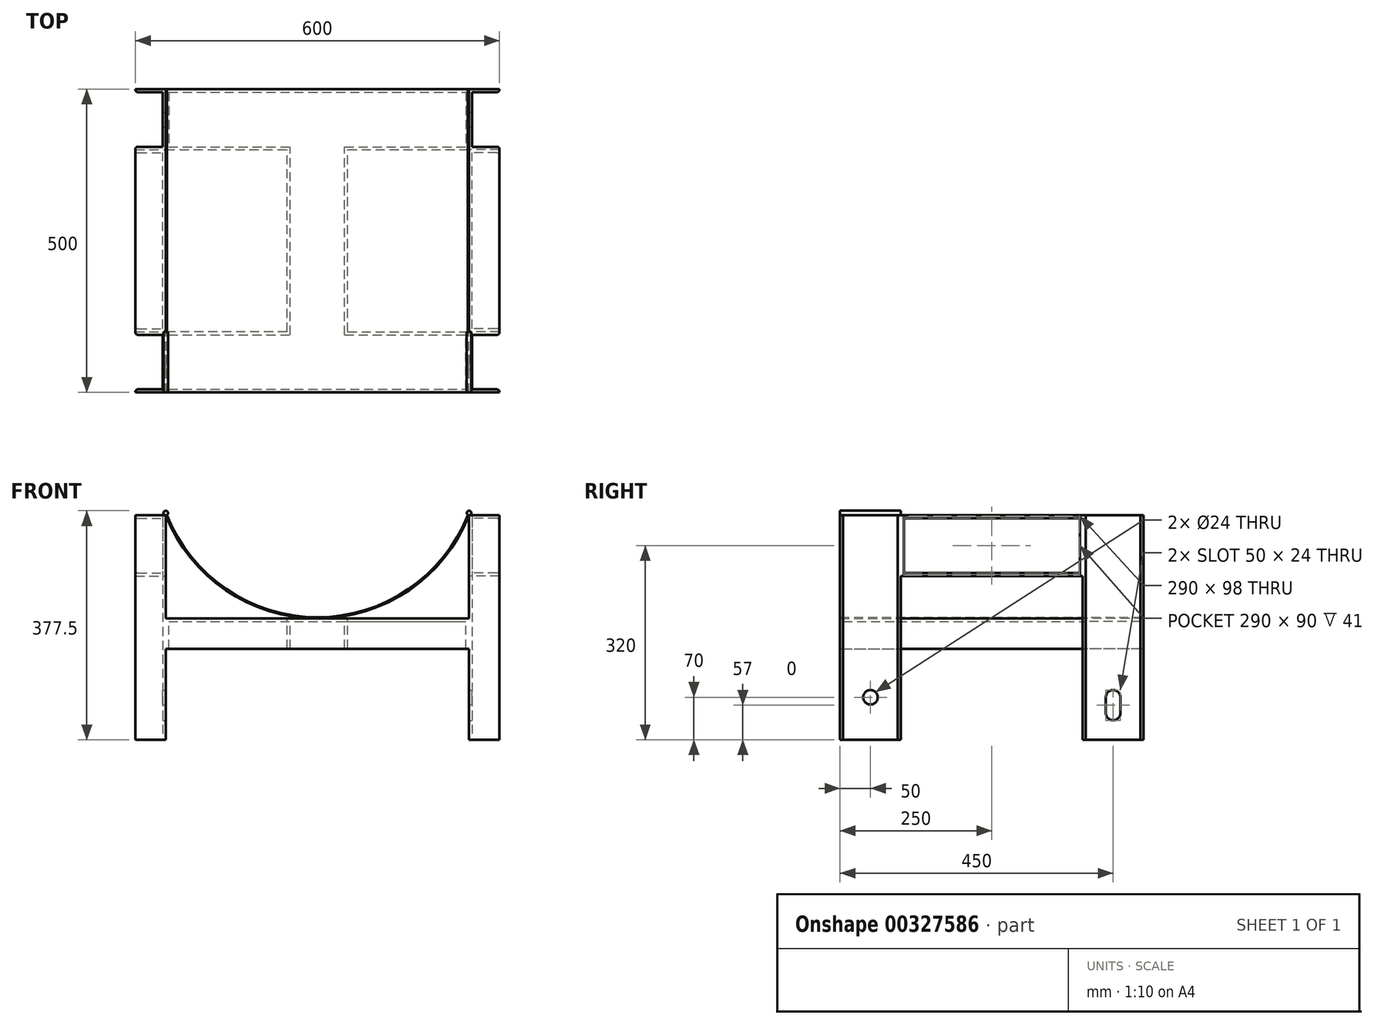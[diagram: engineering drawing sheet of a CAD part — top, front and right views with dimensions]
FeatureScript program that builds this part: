
annotation { "Feature Type Name" : "Feature", "Feature Type Description" : "" }
export const myFeature = defineFeature(function(context is Context, id is Id, definition is map)
    precondition{}
    {
        {
            var Q0;
            Q0=qCreatedBy(makeId("Top.planeOp"),FACE);
            var sketch = newSketch(context, id + "F0", { "sketchPlane" : qUnion([Q0])});
            skLineSegment(sketch, "E0.bottom", {"start": v(250, 250) * mm, "end": v(-250, 250) * mm, "construction": true});
            skLineSegment(sketch, "E0.top", {"start": v(250, -250) * mm, "end": v(-250, -250) * mm, "construction": true});
            skLineSegment(sketch, "E0.left", {"start": v(250, 250) * mm, "end": v(250, -250) * mm, "construction": true});
            skLineSegment(sketch, "E0.right", {"start": v(-250, 250) * mm, "end": v(-250, -250) * mm, "construction": true});
            skPoint(sketch, "E0.middle", {"position": v(0, 0) * mm});
            skLineSegment(sketch, "E1.bottom", {"start": v(-250, 250) * mm, "end": v(250, 250) * mm});
            skLineSegment(sketch, "E1.top", {"start": v(-250, 150) * mm, "end": v(250, 150) * mm});
            skLineSegment(sketch, "E1.left", {"start": v(-250, 250) * mm, "end": v(-250, 150) * mm});
            skLineSegment(sketch, "E1.right", {"start": v(250, 250) * mm, "end": v(250, 150) * mm});
            skLineSegment(sketch, "E2", {"start": v(0, 0) * mm, "end": v(0, 150) * mm, "construction": true});
            skLineSegment(sketch, "E3.bottom", {"start": v(50, 0) * mm, "end": v(-50, 0) * mm});
            skLineSegment(sketch, "E3.top", {"start": v(50, 150) * mm, "end": v(-50, 150) * mm});
            skLineSegment(sketch, "E3.left", {"start": v(50, 0) * mm, "end": v(50, 150) * mm});
            skLineSegment(sketch, "E3.right", {"start": v(-50, 0) * mm, "end": v(-50, 150) * mm});
            skPoint(sketch, "E3.middle", {"position": v(0, 75) * mm});
            skLineSegment(sketch, "E4.MirrorCS", {"start": v(50, 0) * mm, "end": v(50, -150) * mm});
            skLineSegment(sketch, "E5.MirrorCS", {"start": v(-50, 0) * mm, "end": v(-50, -150) * mm});
            skLineSegment(sketch, "E6.MirrorCS", {"start": v(50, -150) * mm, "end": v(-50, -150) * mm});
            skLineSegment(sketch, "E7.MirrorCS", {"start": v(-250, -150) * mm, "end": v(250, -150) * mm});
            skLineSegment(sketch, "E8.MirrorCS", {"start": v(-250, -250) * mm, "end": v(250, -250) * mm});
            skLineSegment(sketch, "E9.MirrorCS", {"start": v(-250, -250) * mm, "end": v(-250, -150) * mm});
            skLineSegment(sketch, "E10.MirrorCS", {"start": v(250, -250) * mm, "end": v(250, -150) * mm});
            skLineSegment(sketch, "E11.bottom", {"start": v(250, -250) * mm, "end": v(300, -250) * mm});
            skLineSegment(sketch, "E11.top", {"start": v(250, -150) * mm, "end": v(300, -150) * mm});
            skLineSegment(sketch, "E11.right", {"start": v(300, -250) * mm, "end": v(300, -249) * mm});
            skLineSegment(sketch, "E12", {"start": v(296, -155) * mm, "end": v(255, -155) * mm});
            skLineSegment(sketch, "E13", {"start": v(255, -155) * mm, "end": v(255, -245) * mm});
            skLineSegment(sketch, "E14", {"start": v(255, -245) * mm, "end": v(296, -245) * mm});
            skLineSegment(sketch, "E15.trimOffspring", {"start": v(300, -151) * mm, "end": v(300, -150) * mm});
            skPoint(sketch, "E16.visualSharp", {"position": v(300, -155) * mm});
            skArc(sketch, "E16.filletArc", {"start": v(296, -155) * mm, "mid": v(298.83, -153.83) * mm, "end": v(300, -151) * mm});
            skPoint(sketch, "E17.visualSharp", {"position": v(300, -245) * mm});
            skArc(sketch, "E17.filletArc", {"start": v(300, -249) * mm, "mid": v(298.83, -246.17) * mm, "end": v(296, -245) * mm});
            skLineSegment(sketch, "E18.MirrorCS", {"start": v(255, 155) * mm, "end": v(255, 245) * mm});
            skLineSegment(sketch, "E19.MirrorCS", {"start": v(250, 150) * mm, "end": v(300, 150) * mm});
            skLineSegment(sketch, "E20.MirrorCS", {"start": v(296, 155) * mm, "end": v(255, 155) * mm});
            skLineSegment(sketch, "E21.MirrorCS", {"start": v(250, 250) * mm, "end": v(300, 250) * mm});
            skLineSegment(sketch, "E22.MirrorCS", {"start": v(255, 245) * mm, "end": v(296, 245) * mm});
            skArc(sketch, "E23.MirrorCS", {"start": v(300, 249) * mm, "mid": v(298.83, 246.17) * mm, "end": v(296, 245) * mm});
            skLineSegment(sketch, "E24.MirrorCS", {"start": v(300, 250) * mm, "end": v(300, 249) * mm});
            skArc(sketch, "E25.MirrorCS", {"start": v(296, 155) * mm, "mid": v(298.83, 153.83) * mm, "end": v(300, 151) * mm});
            skLineSegment(sketch, "E26.MirrorCS", {"start": v(300, 151) * mm, "end": v(300, 150) * mm});
            skLineSegment(sketch, "E27.MirrorCS", {"start": v(-250, 150) * mm, "end": v(-300, 150) * mm});
            skLineSegment(sketch, "E28.MirrorCS", {"start": v(-296, 155) * mm, "end": v(-255, 155) * mm});
            skLineSegment(sketch, "E29.MirrorCS", {"start": v(-250, 250) * mm, "end": v(-300, 250) * mm});
            skLineSegment(sketch, "E30.MirrorCS", {"start": v(-255, 245) * mm, "end": v(-296, 245) * mm});
            skLineSegment(sketch, "E31.MirrorCS", {"start": v(-255, 155) * mm, "end": v(-255, 245) * mm});
            skArc(sketch, "E32.MirrorCS", {"start": v(-296, 155) * mm, "mid": v(-298.83, 153.83) * mm, "end": v(-300, 151) * mm});
            skArc(sketch, "E33.MirrorCS", {"start": v(-300, 249) * mm, "mid": v(-298.83, 246.17) * mm, "end": v(-296, 245) * mm});
            skLineSegment(sketch, "E34.MirrorCS", {"start": v(-300, 250) * mm, "end": v(-300, 249) * mm});
            skLineSegment(sketch, "E35.MirrorCS", {"start": v(-300, 151) * mm, "end": v(-300, 150) * mm});
            skLineSegment(sketch, "E36.MirrorCS", {"start": v(-250, -250) * mm, "end": v(-300, -250) * mm});
            skLineSegment(sketch, "E37.MirrorCS", {"start": v(-255, -245) * mm, "end": v(-296, -245) * mm});
            skLineSegment(sketch, "E38.MirrorCS", {"start": v(-296, -155) * mm, "end": v(-255, -155) * mm});
            skLineSegment(sketch, "E39.MirrorCS", {"start": v(-250, -150) * mm, "end": v(-300, -150) * mm});
            skArc(sketch, "E40.MirrorCS", {"start": v(-300, -249) * mm, "mid": v(-298.83, -246.17) * mm, "end": v(-296, -245) * mm});
            skLineSegment(sketch, "E41.MirrorCS", {"start": v(-300, -250) * mm, "end": v(-300, -249) * mm});
            skArc(sketch, "E42.MirrorCS", {"start": v(-296, -155) * mm, "mid": v(-298.83, -153.83) * mm, "end": v(-300, -151) * mm});
            skLineSegment(sketch, "E43.MirrorCS", {"start": v(-300, -151) * mm, "end": v(-300, -150) * mm});
            skLineSegment(sketch, "E44.MirrorCS", {"start": v(-255, -155) * mm, "end": v(-255, -245) * mm});
            skSolve(sketch);
        }
        {
            var Q0;
            Q0=makeQuery(id+"F0.imprint","IMPRINT",FACE,{"disambiguationData":[TD([[makeQuery(id+"F0.imprint","IMPRINT",EDGE,{"derivedFrom":sQuery(id+"F0.wireOp",EDGE,"E1.bottom")}),-1.0]])]});
            var Q1;
            Q1=makeQuery(id+"F0.imprint","IMPRINT",FACE,{"disambiguationData":[TD([[makeQuery(id+"F0.imprint","IMPRINT",EDGE,{"derivedFrom":sQuery(id+"F0.wireOp",EDGE,"E3.bottom")}),-1.0]])]});
            var Q2;
            Q2=makeQuery(id+"F0.imprint","IMPRINT",FACE,{"disambiguationData":[TD([[makeQuery(id+"F0.imprint","IMPRINT",EDGE,{"derivedFrom":sQuery(id+"F0.wireOp",EDGE,"E3.bottom")}),1.0]])]});
            var Q3;
            Q3=makeQuery(id+"F0.imprint","IMPRINT",FACE,{"disambiguationData":[TD([[makeQuery(id+"F0.imprint","IMPRINT",EDGE,{"derivedFrom":sQuery(id+"F0.wireOp",EDGE,"E8.MirrorCS")}),1.0]])]});
            extrude(context, id + "F1", {"entities" : qUnion([Q0, Q1, Q2, Q3]), "oppositeDirection" : true, "depth" : 50 * mm});
        }
        {
            var Q0;
            Q0=makeQuery(id+"F1.opExtrude","CAP_FACE",FACE,{"disambiguationData":[OSD([sQuery(id+"F0.wireOp",EDGE,"E1.bottom"),sQuery(id+"F0.wireOp",EDGE,"E1.top"),sQuery(id+"F0.wireOp",EDGE,"E1.left"),sQuery(id+"F0.wireOp",EDGE,"E1.right"),sQuery(id+"F0.wireOp",EDGE,"E3.left"),sQuery(id+"F0.wireOp",EDGE,"E3.right"),sQuery(id+"F0.wireOp",EDGE,"E4.MirrorCS"),sQuery(id+"F0.wireOp",EDGE,"E5.MirrorCS"),sQuery(id+"F0.wireOp",EDGE,"E7.MirrorCS"),sQuery(id+"F0.wireOp",EDGE,"E8.MirrorCS"),sQuery(id+"F0.wireOp",EDGE,"E9.MirrorCS"),sQuery(id+"F0.wireOp",EDGE,"E10.MirrorCS")])],"isStart":false});
            shell(context, id + "F2", {"entities" : qUnion([Q0]), "thickness" : 5 * mm});
        }
        {
            var Q0;
            Q0=makeQuery(id+"F0.imprint","IMPRINT",FACE,{"disambiguationData":[TD([[makeQuery(id+"F0.imprint","IMPRINT",EDGE,{"derivedFrom":sQuery(id+"F0.wireOp",EDGE,"E9.MirrorCS")}),1.0]])]});
            var Q1;
            Q1=makeQuery(id+"F0.imprint","IMPRINT",FACE,{"disambiguationData":[TD([[makeQuery(id+"F0.imprint","IMPRINT",EDGE,{"derivedFrom":sQuery(id+"F0.wireOp",EDGE,"E11.bottom")}),1.0]])]});
            var Q2;
            Q2=makeQuery(id+"F0.imprint","IMPRINT",FACE,{"disambiguationData":[TD([[makeQuery(id+"F0.imprint","IMPRINT",EDGE,{"derivedFrom":sQuery(id+"F0.wireOp",EDGE,"E1.right")}),1.0]])]});
            var Q3;
            Q3=makeQuery(id+"F0.imprint","IMPRINT",FACE,{"disambiguationData":[TD([[makeQuery(id+"F0.imprint","IMPRINT",EDGE,{"derivedFrom":sQuery(id+"F0.wireOp",EDGE,"E1.left")}),-1.0]])]});
            extrude(context, id + "F3", {"entities" : qUnion([Q0, Q1, Q2, Q3]), "depth" : 170 * mm});
        }
        {
            var Q0;
            Q0=makeQuery(id+"F0.imprint","IMPRINT",FACE,{"disambiguationData":[TD([[makeQuery(id+"F0.imprint","IMPRINT",EDGE,{"derivedFrom":sQuery(id+"F0.wireOp",EDGE,"E9.MirrorCS")}),1.0]])]});
            var Q1;
            Q1=makeQuery(id+"F0.imprint","IMPRINT",FACE,{"disambiguationData":[TD([[makeQuery(id+"F0.imprint","IMPRINT",EDGE,{"derivedFrom":sQuery(id+"F0.wireOp",EDGE,"E11.bottom")}),1.0]])]});
            var Q2;
            Q2=makeQuery(id+"F0.imprint","IMPRINT",FACE,{"disambiguationData":[TD([[makeQuery(id+"F0.imprint","IMPRINT",EDGE,{"derivedFrom":sQuery(id+"F0.wireOp",EDGE,"E1.right")}),1.0]])]});
            var Q3;
            Q3=makeQuery(id+"F0.imprint","IMPRINT",FACE,{"disambiguationData":[TD([[makeQuery(id+"F0.imprint","IMPRINT",EDGE,{"derivedFrom":sQuery(id+"F0.wireOp",EDGE,"E1.left")}),-1.0]])]});
            extrude(context, id + "F4", {"entities" : qUnion([Q0, Q1, Q2, Q3]), "oppositeDirection" : true, "depth" : 200 * mm});
        }
        {
            var Q0;
            Q0=makeQuery(id+"F3.opExtrude","SWEPT_BODY",BODY,{"disambiguationData":[OSD([sQuery(id+"F0.wireOp",EDGE,"E11.bottom"),sQuery(id+"F0.wireOp",EDGE,"E11.top"),sQuery(id+"F0.wireOp",EDGE,"E10.MirrorCS"),sQuery(id+"F0.wireOp",EDGE,"E11.right"),sQuery(id+"F0.wireOp",EDGE,"E12"),sQuery(id+"F0.wireOp",EDGE,"E13"),sQuery(id+"F0.wireOp",EDGE,"E14"),sQuery(id+"F0.wireOp",EDGE,"E15.trimOffspring"),sQuery(id+"F0.wireOp",EDGE,"E16.filletArc"),sQuery(id+"F0.wireOp",EDGE,"E17.filletArc")])]});
            var Q1;
            Q1=makeQuery(id+"F4.opExtrude","SWEPT_BODY",BODY,{"disambiguationData":[OSD([sQuery(id+"F0.wireOp",EDGE,"E11.bottom"),sQuery(id+"F0.wireOp",EDGE,"E11.top"),sQuery(id+"F0.wireOp",EDGE,"E10.MirrorCS"),sQuery(id+"F0.wireOp",EDGE,"E11.right"),sQuery(id+"F0.wireOp",EDGE,"E12"),sQuery(id+"F0.wireOp",EDGE,"E13"),sQuery(id+"F0.wireOp",EDGE,"E14"),sQuery(id+"F0.wireOp",EDGE,"E15.trimOffspring"),sQuery(id+"F0.wireOp",EDGE,"E16.filletArc"),sQuery(id+"F0.wireOp",EDGE,"E17.filletArc")])]});
            var Q2;
            Q2=makeQuery(id+"F3.opExtrude","SWEPT_BODY",BODY,{"disambiguationData":[OSD([sQuery(id+"F0.wireOp",EDGE,"E1.right"),sQuery(id+"F0.wireOp",EDGE,"E18.MirrorCS"),sQuery(id+"F0.wireOp",EDGE,"E19.MirrorCS"),sQuery(id+"F0.wireOp",EDGE,"E20.MirrorCS"),sQuery(id+"F0.wireOp",EDGE,"E21.MirrorCS"),sQuery(id+"F0.wireOp",EDGE,"E22.MirrorCS"),sQuery(id+"F0.wireOp",EDGE,"E23.MirrorCS"),sQuery(id+"F0.wireOp",EDGE,"E24.MirrorCS"),sQuery(id+"F0.wireOp",EDGE,"E25.MirrorCS"),sQuery(id+"F0.wireOp",EDGE,"E26.MirrorCS")])]});
            var Q3;
            Q3=makeQuery(id+"F4.opExtrude","SWEPT_BODY",BODY,{"disambiguationData":[OSD([sQuery(id+"F0.wireOp",EDGE,"E1.right"),sQuery(id+"F0.wireOp",EDGE,"E18.MirrorCS"),sQuery(id+"F0.wireOp",EDGE,"E19.MirrorCS"),sQuery(id+"F0.wireOp",EDGE,"E20.MirrorCS"),sQuery(id+"F0.wireOp",EDGE,"E21.MirrorCS"),sQuery(id+"F0.wireOp",EDGE,"E22.MirrorCS"),sQuery(id+"F0.wireOp",EDGE,"E23.MirrorCS"),sQuery(id+"F0.wireOp",EDGE,"E24.MirrorCS"),sQuery(id+"F0.wireOp",EDGE,"E25.MirrorCS"),sQuery(id+"F0.wireOp",EDGE,"E26.MirrorCS")])]});
            var Q4;
            Q4=makeQuery(id+"F3.opExtrude","SWEPT_BODY",BODY,{"disambiguationData":[OSD([sQuery(id+"F0.wireOp",EDGE,"E9.MirrorCS"),sQuery(id+"F0.wireOp",EDGE,"E36.MirrorCS"),sQuery(id+"F0.wireOp",EDGE,"E37.MirrorCS"),sQuery(id+"F0.wireOp",EDGE,"E38.MirrorCS"),sQuery(id+"F0.wireOp",EDGE,"E39.MirrorCS"),sQuery(id+"F0.wireOp",EDGE,"E40.MirrorCS"),sQuery(id+"F0.wireOp",EDGE,"E41.MirrorCS"),sQuery(id+"F0.wireOp",EDGE,"E42.MirrorCS"),sQuery(id+"F0.wireOp",EDGE,"E43.MirrorCS"),sQuery(id+"F0.wireOp",EDGE,"E44.MirrorCS")])]});
            var Q5;
            Q5=makeQuery(id+"F4.opExtrude","SWEPT_BODY",BODY,{"disambiguationData":[OSD([sQuery(id+"F0.wireOp",EDGE,"E9.MirrorCS"),sQuery(id+"F0.wireOp",EDGE,"E36.MirrorCS"),sQuery(id+"F0.wireOp",EDGE,"E37.MirrorCS"),sQuery(id+"F0.wireOp",EDGE,"E38.MirrorCS"),sQuery(id+"F0.wireOp",EDGE,"E39.MirrorCS"),sQuery(id+"F0.wireOp",EDGE,"E40.MirrorCS"),sQuery(id+"F0.wireOp",EDGE,"E41.MirrorCS"),sQuery(id+"F0.wireOp",EDGE,"E42.MirrorCS"),sQuery(id+"F0.wireOp",EDGE,"E43.MirrorCS"),sQuery(id+"F0.wireOp",EDGE,"E44.MirrorCS")])]});
            var Q6;
            Q6=makeQuery(id+"F4.opExtrude","SWEPT_BODY",BODY,{"disambiguationData":[OSD([sQuery(id+"F0.wireOp",EDGE,"E1.left"),sQuery(id+"F0.wireOp",EDGE,"E27.MirrorCS"),sQuery(id+"F0.wireOp",EDGE,"E28.MirrorCS"),sQuery(id+"F0.wireOp",EDGE,"E29.MirrorCS"),sQuery(id+"F0.wireOp",EDGE,"E30.MirrorCS"),sQuery(id+"F0.wireOp",EDGE,"E31.MirrorCS"),sQuery(id+"F0.wireOp",EDGE,"E32.MirrorCS"),sQuery(id+"F0.wireOp",EDGE,"E33.MirrorCS"),sQuery(id+"F0.wireOp",EDGE,"E34.MirrorCS"),sQuery(id+"F0.wireOp",EDGE,"E35.MirrorCS")])]});
            var Q7;
            Q7=makeQuery(id+"F3.opExtrude","SWEPT_BODY",BODY,{"disambiguationData":[OSD([sQuery(id+"F0.wireOp",EDGE,"E1.left"),sQuery(id+"F0.wireOp",EDGE,"E27.MirrorCS"),sQuery(id+"F0.wireOp",EDGE,"E28.MirrorCS"),sQuery(id+"F0.wireOp",EDGE,"E29.MirrorCS"),sQuery(id+"F0.wireOp",EDGE,"E30.MirrorCS"),sQuery(id+"F0.wireOp",EDGE,"E31.MirrorCS"),sQuery(id+"F0.wireOp",EDGE,"E32.MirrorCS"),sQuery(id+"F0.wireOp",EDGE,"E33.MirrorCS"),sQuery(id+"F0.wireOp",EDGE,"E34.MirrorCS"),sQuery(id+"F0.wireOp",EDGE,"E35.MirrorCS")])]});
            var Q8;
            Q8=makeQuery(id+"F1.opExtrude","SWEPT_BODY",BODY,{"disambiguationData":[OSD([sQuery(id+"F0.wireOp",EDGE,"E1.bottom"),sQuery(id+"F0.wireOp",EDGE,"E1.top"),sQuery(id+"F0.wireOp",EDGE,"E1.left"),sQuery(id+"F0.wireOp",EDGE,"E1.right"),sQuery(id+"F0.wireOp",EDGE,"E3.left"),sQuery(id+"F0.wireOp",EDGE,"E3.right"),sQuery(id+"F0.wireOp",EDGE,"E4.MirrorCS"),sQuery(id+"F0.wireOp",EDGE,"E5.MirrorCS"),sQuery(id+"F0.wireOp",EDGE,"E7.MirrorCS"),sQuery(id+"F0.wireOp",EDGE,"E8.MirrorCS"),sQuery(id+"F0.wireOp",EDGE,"E9.MirrorCS"),sQuery(id+"F0.wireOp",EDGE,"E10.MirrorCS")])]});
            booleanBodies(context, id + "F5", {"operationType" : BooleanOperationType.UNION, "tools" : qUnion([Q0, Q1, Q2, Q3, Q4, Q5, Q6, Q7, Q8])});
        }
        {
            var Q0;
            Q0=qCreatedBy(makeId("Front.planeOp"),FACE);
            var sketch = newSketch(context, id + "F6", { "sketchPlane" : qUnion([Q0])});
            skLineSegment(sketch, "E45.bottom", {"start": v(250, 170) * mm, "end": v(-250, 170) * mm, "construction": true});
            skLineSegment(sketch, "E45.top", {"start": v(250, -170) * mm, "end": v(-250, -170) * mm, "construction": true});
            skLineSegment(sketch, "E45.left", {"start": v(250, 170) * mm, "end": v(250, -170) * mm, "construction": true});
            skLineSegment(sketch, "E45.right", {"start": v(-250, 170) * mm, "end": v(-250, -170) * mm, "construction": true});
            skPoint(sketch, "E45.middle", {"position": v(0, 0) * mm});
            skArc(sketch, "E46", {"start": v(-250, 170) * mm, "mid": v(0, 0) * mm, "end": v(250, 170) * mm});
            skArc(sketch, "E47.0", {"start": v(-247.85, 170) * mm, "mid": v(0, 2) * mm, "end": v(247.85, 170) * mm});
            skLineSegment(sketch, "E48", {"start": v(247.85, 170) * mm, "end": v(250, 170) * mm});
            skLineSegment(sketch, "E49", {"start": v(-250, 170) * mm, "end": v(-247.85, 170) * mm});
            skSolve(sketch);
        }
        {
            var Q0;
            Q0=makeQuery(id+"F6.imprint","IMPRINT",FACE,{"disambiguationData":[TD([[makeQuery(id+"F6.imprint","IMPRINT",EDGE,{"derivedFrom":sQuery(id+"F6.wireOp",EDGE,"E46")}),1.0]])]});
            var Q1;
            Q1=makeQuery(id+"F6.imprint","IMPRINT",FACE,{"disambiguationData":[TD([[makeQuery(id+"F6.imprint","IMPRINT",EDGE,{"derivedFrom":sQuery(id+"F6.wireOp",EDGE,"KrNz5f9j-idMk-tH8w-1q6d-Px5I6zzqWWuj")}),1.0]])]});
            var Q2;
            Q2=makeQuery(id+"F6.imprint","IMPRINT",FACE,{"disambiguationData":[TD([[makeQuery(id+"F6.imprint","IMPRINT",EDGE,{"derivedFrom":sQuery(id+"F6.wireOp",EDGE,"515c8cf5-25ff-4abc-af07-5d9691053d920.MirrorC")}),-1.0]])]});
            extrude(context, id + "F7", {"entities" : qUnion([Q0, Q1, Q2]), "operationType" : NewBodyOperationType.ADD, "endBound" : BoundingType.SYMMETRIC, "depth" : 500 * mm});
        }
        {
            var Q0;
            Q0=makeQuery(id+"F3.opExtrude","SWEPT_FACE",FACE,{"disambiguationData":[OSD([sQuery(id+"F0.wireOp",EDGE,"E10.MirrorCS")])]});
            var sketch = newSketch(context, id + "F8", { "sketchPlane" : qUnion([Q0])});
            skLineSegment(sketch, "E50.bottom", {"start": v(150, 170) * mm, "end": v(-150, 170) * mm});
            skLineSegment(sketch, "E50.top", {"start": v(150, 70) * mm, "end": v(-150, 70) * mm});
            skLineSegment(sketch, "E50.left", {"start": v(150, 170) * mm, "end": v(150, 70) * mm});
            skLineSegment(sketch, "E50.right", {"start": v(-150, 170) * mm, "end": v(-150, 70) * mm});
            skSolve(sketch);
        }
        {
            var Q0;
            Q0=makeQuery(id+"F8.imprint","IMPRINT",FACE,{"disambiguationData":[TD([[makeQuery(id+"F8.imprint","IMPRINT",EDGE,{"derivedFrom":sQuery(id+"F8.wireOp",EDGE,"E50.bottom")}),1.0]])]});
            extrude(context, id + "F9", {"entities" : qUnion([Q0]), "oppositeDirection" : true, "depth" : 50 * mm});
        }
        {
            var Q0;
            Q0=makeQuery(id+"F9.opExtrude","CAP_FACE",FACE,{"disambiguationData":[OSD([sQuery(id+"F8.wireOp",EDGE,"E50.bottom"),sQuery(id+"F8.wireOp",EDGE,"E50.top"),sQuery(id+"F8.wireOp",EDGE,"E50.left"),sQuery(id+"F8.wireOp",EDGE,"E50.right")])],"isStart":false});
            shell(context, id + "F10", {"entities" : qUnion([Q0]), "thickness" : 5 * mm});
        }
        {
            var Q0;
            {var subQ0=sQuery(id+"F8.wireOp",EDGE,"E50.bottom");Q0=makeQuery(id+"F10.opShell","OFFSET_EDGE",EDGE,{"disambiguationData":[OSD([subQ0]),TDD([makeQuery(id+"F9.opExtrude","CAP_EDGE",EDGE,{"disambiguationData":[OSD([subQ0])],"isStart":false})])]});}
            var Q1;
            {var subQ0=sQuery(id+"F8.wireOp",EDGE,"E50.top");Q1=makeQuery(id+"F10.opShell","OFFSET_EDGE",EDGE,{"disambiguationData":[OSD([subQ0]),TDD([makeQuery(id+"F9.opExtrude","CAP_EDGE",EDGE,{"disambiguationData":[OSD([subQ0])],"isStart":false})])]});}
            fillet(context, id + "F11", {"entities" : qUnion([Q0, Q1]), "radius" : 4 * mm, "tangentPropagation" : true, "allowEdgeOverflow" : false});
        }
        {
            var Q0;
            Q0=makeQuery(id+"F9.opExtrude","SWEPT_BODY",BODY,{"disambiguationData":[OSD([sQuery(id+"F8.wireOp",EDGE,"E50.bottom"),sQuery(id+"F8.wireOp",EDGE,"E50.top"),sQuery(id+"F8.wireOp",EDGE,"E50.left"),sQuery(id+"F8.wireOp",EDGE,"E50.right")])]});
            var Q1;
            Q1=qCreatedBy(makeId("Right.planeOp"),FACE);
            mirror(context, id + "F12", {"operationType" : NewBodyOperationType.ADD, "entities" : qUnion([Q0]), "mirrorPlane" : qUnion([Q1])});
        }
        {
            var Q0;
            {var subQ0=sQuery(id+"F0.wireOp",EDGE,"E13");Q0=makeQuery(id+"F5.opBoolean","MERGE",FACE,{"derivedFrom":[makeQuery(id+"F3.opExtrude","SWEPT_FACE",FACE,{"disambiguationData":[OSD([subQ0])]}),makeQuery(id+"F4.opExtrude","SWEPT_FACE",FACE,{"disambiguationData":[OSD([subQ0])]})]});}
            var sketch = newSketch(context, id + "F13", { "sketchPlane" : qUnion([Q0])});
            skLineSegment(sketch, "E51", {"start": v(-200, -200) * mm, "end": v(-200, -130) * mm, "construction": true});
            skPoint(sketch, "E52", {"position": v(-200, -130) * mm});
            skLineSegment(sketch, "E53", {"start": v(-200, -200) * mm, "end": v(200, -200) * mm, "construction": true});
            skLineSegment(sketch, "E54", {"start": v(200, -200) * mm, "end": v(200, -143) * mm, "construction": true});
            skPoint(sketch, "E55", {"position": v(200, -143) * mm});
            skLineSegment(sketch, "E56.bottom", {"start": v(212, -118) * mm, "end": v(188, -118) * mm});
            skLineSegment(sketch, "E56.top", {"start": v(212, -168) * mm, "end": v(188, -168) * mm});
            skLineSegment(sketch, "E56.left", {"start": v(212, -118) * mm, "end": v(212, -168) * mm});
            skLineSegment(sketch, "E56.right", {"start": v(188, -118) * mm, "end": v(188, -168) * mm});
            skLineSegment(sketch, "E57", {"start": v(200, -118) * mm, "end": v(200, -130) * mm, "construction": true});
            skPoint(sketch, "E58.orphan", {"position": v(212, -130) * mm});
            skPoint(sketch, "E59.0.end.orphan", {"position": v(188, -130) * mm});
            skArc(sketch, "E60", {"start": v(212, -130) * mm, "mid": v(200, -118) * mm, "end": v(188, -130) * mm});
            skLineSegment(sketch, "E61", {"start": v(188, -143) * mm, "end": v(212, -143) * mm, "construction": true});
            skArc(sketch, "E62.MirrorCS", {"start": v(212, -156) * mm, "mid": v(200, -168) * mm, "end": v(188, -156) * mm});
            skSolve(sketch);
        }
        {
            var Q0;
            {var subQ0=sQuery(id+"F13.wireOp",EDGE,"E60");var subQ6=sQuery(id+"F13.wireOp",EDGE,"E56.left");var subQ7=makeQuery(id+"F13.imprint","INTERSECT",VERTEX,{"derivedFrom":[subQ6,subQ0]});Q0=makeQuery(id+"F13.imprint","IMPRINT",FACE,{"disambiguationData":[TD([[makeQuery(id+"F13.imprint","IMPRINT",EDGE,{"disambiguationData":[TD([[subQ7,-1.0]])],"derivedFrom":subQ6}),-1.0]])]});}
            extrude(context, id + "F14", {"entities" : qUnion([Q0]), "operationType" : NewBodyOperationType.REMOVE, "endBound" : BoundingType.THROUGH_ALL, "oppositeDirection" : true, "depth" : 25 * mm});
        }
        {
            var Q0;
            Q0=sQuery(id+"F13.wireOp",VERTEX,"E52");
            var Q1;
            Q1=makeQuery(id+"F3.opExtrude","SWEPT_BODY",BODY,{"disambiguationData":[OSD([sQuery(id+"F0.wireOp",EDGE,"E11.bottom"),sQuery(id+"F0.wireOp",EDGE,"E11.top"),sQuery(id+"F0.wireOp",EDGE,"E10.MirrorCS"),sQuery(id+"F0.wireOp",EDGE,"E11.right"),sQuery(id+"F0.wireOp",EDGE,"E12"),sQuery(id+"F0.wireOp",EDGE,"E13"),sQuery(id+"F0.wireOp",EDGE,"E14"),sQuery(id+"F0.wireOp",EDGE,"E15.trimOffspring"),sQuery(id+"F0.wireOp",EDGE,"E16.filletArc"),sQuery(id+"F0.wireOp",EDGE,"E17.filletArc")])]});
            hole(context, id + "F15", {"style" : HoleStyle.SIMPLE, "endStyle" : HoleEndStyle.THROUGH, "holeDiameter" : 24 * mm, "tappedDepth" : 12 * mm, "tapClearance" : 3, "locations" : qUnion([Q0]), "scope" : qUnion([Q1])});
        }
        {
            var Q0;
            {var subQ0=sQuery(id+"F0.wireOp",EDGE,"E36.MirrorCS");var subQ1=sQuery(id+"F0.wireOp",EDGE,"E11.bottom");Q0=makeQuery(id+"F5.opBoolean","MERGE",FACE,{"derivedFrom":[makeQuery(id+"F1.opExtrude","SWEPT_FACE",FACE,{"disambiguationData":[OSD([sQuery(id+"F0.wireOp",EDGE,"E8.MirrorCS")])]}),makeQuery(id+"F3.opExtrude","SWEPT_FACE",FACE,{"disambiguationData":[OSD([subQ1])]}),makeQuery(id+"F3.opExtrude","SWEPT_FACE",FACE,{"disambiguationData":[OSD([subQ0])]}),makeQuery(id+"F4.opExtrude","SWEPT_FACE",FACE,{"disambiguationData":[OSD([subQ1])]}),makeQuery(id+"F4.opExtrude","SWEPT_FACE",FACE,{"disambiguationData":[OSD([subQ0])]})]});}
            var sketch = newSketch(context, id + "F16", { "sketchPlane" : qUnion([Q0])});
            skLineSegment(sketch, "E63", {"start": v(-250, 170) * mm, "end": v(-250, 177.5) * mm, "construction": true});
            skCircle(sketch, "E64", {"center": v(-250, 173.75) * mm, "radius": 3.75 * mm});
            skCircle(sketch, "E65.MirrorC", {"center": v(250, 173.75) * mm, "radius": 3.75 * mm});
            skSolve(sketch);
        }
        {
            var Q0;
            Q0 = qSketchRegion(id + "F16", true);
            extrude(context, id + "F17", {"entities" : qUnion([Q0]), "oppositeDirection" : true, "depth" : 100 * mm});
        }
    });
